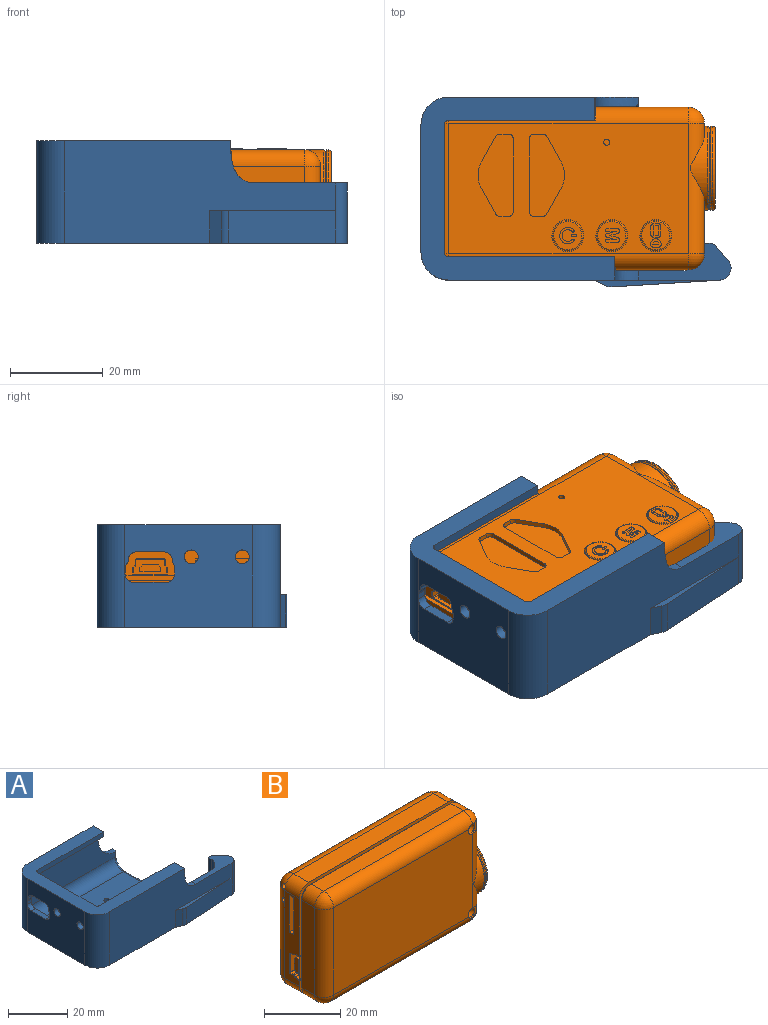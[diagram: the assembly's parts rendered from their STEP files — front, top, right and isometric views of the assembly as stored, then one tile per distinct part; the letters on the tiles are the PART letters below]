
ASSEMBLY  parts=2 mates=1
PART A: 69 faces, bbox 66.9x41x22.1 mm
  f0: plane 27.5x22.1mm, normal (-1,0,0), area 529.3mm2, adj f2,f4,f40,f41,f57,f58,f59,f60
  f1: plane 27.5x11.1mm, normal (1,0,0), area 226.8mm2, adj f33,f36,f37,f46,f57,f58,f59,f60
  f2: plane 66.93x40.96mm, normal (0,0,-1), area 1888.3mm2, adj f0,f6,f7,f8,f10,f11,f12,f13
  f3: plane 40x27.5mm, normal (0,0,1), area 1079.5mm2, adj f28,f29,f30,f31,f34,f37,f39,f51
  f4: plane 41.8x39.5mm, normal (0,0,1), area 529.1mm2, adj f0,f5,f6,f7,f21,f23,f24,f25
  f5: extruded ~5x2.17mm, area 10.8mm2, adj f4,f6,f22,f25,f48
  f6: plane 41.01x22.1mm, normal (0,1,0), area 794.4mm2, adj f2,f4,f5,f8,f22,f41
  f7: plane 58.44x22.1mm, normal (0,-1,0), area 902.9mm2, adj f2,f4,f12,f17,f19,f20,f21,f40
  f8: plane 29.43x7.84mm, normal (1,0,0), area 41.6mm2, adj f2,f6,f22,f32,f49,f50,f51
  f9: plane 40.01x11.11mm, normal (0,-1,0), area 388.3mm2, adj f22,f33,f34,f48,f49
  f10: plane 50.17x17.31mm, normal (0,1,0), area 589.1mm2, adj f2,f13,f17,f21,f26,f36,f39,f44
  f11: plane 13x3.57mm, normal (0.77,0.64,0), area 60.6mm2, adj f2,f12,f16,f17
  f12: cylinder r=2.63mm len=13mm, axis (0,0,-1), area 66.5mm2, adj f2,f7,f11,f17,f18
  f13: cylinder r=4.94mm len=13mm, axis (0,0,-1), area 96.9mm2, adj f2,f10,f14,f17
  f14: plane 13x1.37mm, normal (-1,0,0), area 17.8mm2, adj f2,f13,f15,f17
  f15: plane 13x1.07mm, normal (0,1,0), area 13.9mm2, adj f2,f14,f16,f17
  f16: cylinder r=2mm len=13mm, axis (0,0,-1), area 22.7mm2, adj f2,f11,f15,f17
  f17: plane 19.93x8mm, normal (0,0,1), area 69.6mm2, adj f7,f10,f11,f12,f13,f14,f15,f16
  f18: plane 23.18x7mm, normal (0.06,-1,0), area 162.6mm2, adj f2,f12,f20,f56
  f19: plane 7x2.43mm, normal (-0.43,-0.9,0), area 18.9mm2, adj f2,f7,f20,f56
  f20: plane 27.1x1.46mm, normal (0,0,1), area 20.3mm2, adj f7,f18,f19,f56
  f21: extruded ~9.1x5.21mm, area 31.7mm2, adj f4,f7,f10,f17,f24,f44
  f22: extruded ~12.09x9.37mm, area 35.6mm2, adj f5,f6,f8,f9,f48,f49
  f23: plane 27.5x2mm, normal (1,0,0), area 55mm2, adj f4,f42,f43,f46
  f24: plane 35.83x2.01mm, normal (0,1,0), area 71.6mm2, adj f4,f21,f42,f44
  f25: plane 31.62x2.01mm, normal (0,-1,0), area 63.1mm2, adj f4,f5,f43,f48
  f26: cylinder r=2.04mm len=6mm, axis (0,0,-1), area 14.1mm2, adj f2,f10,f27,f54,f55
  f27: plane 1x0.95mm, normal (0,-1,0), area 0.9mm2, adj f2,f26,f32,f53
  f28: cylinder r=1mm len=2mm, axis (0,0,-1), area 12.6mm2, adj f2,f3
  f29: cylinder r=1mm len=2mm, axis (0,0,-1), area 12.6mm2, adj f2,f3
  f30: cylinder r=1mm len=2mm, axis (0,0,-1), area 12.6mm2, adj f2,f3
  f31: cylinder r=1mm len=2mm, axis (0,0,-1), area 12.6mm2, adj f2,f3
  f32: cylinder r=4mm len=4mm, axis (0,0,1), area 6.3mm2, adj f2,f8,f27,f52
  f33: cylinder r=4mm len=11.1mm, axis (0,0,-1), area 69.7mm2, adj f1,f9,f35,f47
  f34: cylinder r=4mm len=40mm, axis (-1,0,0), area 251.3mm2, adj f3,f9,f35,f50
  f35: sphere r=4mm, area 25.1mm2, adj f33,f34,f37
  f36: cylinder r=4mm len=11.1mm, axis (0,0,1), area 69.7mm2, adj f1,f10,f38,f45
  f37: cylinder r=4mm len=27.5mm, axis (0,-1,0), area 172.8mm2, adj f1,f3,f35,f38
  f38: sphere r=4mm, area 25.1mm2, adj f36,f37,f39
  f39: cylinder r=4mm len=36.05mm, axis (1,0,0), area 213.1mm2, adj f3,f10,f38,f55
  f40: cylinder r=6mm len=22.1mm, axis (0,0,-1), area 208.3mm2, adj f0,f2,f4,f7
  f41: cylinder r=6mm len=22.1mm, axis (0,0,1), area 208.3mm2, adj f0,f2,f4,f6
  f42: cylinder r=1mm len=2mm, axis (0,0,-1), area 3.1mm2, adj f4,f23,f24,f45
  f43: cylinder r=1mm len=2mm, axis (0,0,1), area 3.1mm2, adj f4,f23,f25,f47
  f44: cylinder r=3mm len=36.24mm, axis (-1,0,0), area 169.3mm2, adj f10,f21,f24,f45
  f45: torus R=1mm, axis (0,0,-1), area 21.5mm2, adj f36,f42,f44,f46
  f46: cylinder r=3mm len=27.5mm, axis (0,1,0), area 129.6mm2, adj f1,f23,f45,f47
  f47: torus R=1mm, axis (0,0,-1), area 21.5mm2, adj f33,f43,f46,f48
  f48: cylinder r=3mm len=31.83mm, axis (1,0,0), area 149.4mm2, adj f5,f9,f22,f25,f47
  f49: cylinder r=1mm len=1.95mm, axis (0,0,1), area 3mm2, adj f8,f9,f22,f50
  f50: torus R=5mm, axis (1,0,0), area 10.8mm2, adj f8,f34,f49,f51
  f51: cylinder r=1mm len=23.43mm, axis (0,1,0), area 36.8mm2, adj f3,f8,f50,f52
  f52: torus R=3mm, axis (0,0,-1), area 9mm2, adj f3,f32,f51,f53
  f53: cylinder r=1mm len=1mm, axis (-1,0,0), area 1.5mm2, adj f3,f27,f52,f54
  f54: torus R=3.04mm, axis (0,0,-1), area 3.3mm2, adj f3,f26,f53,f55
  f55: bspline ~5x4.37mm, area 6.9mm2, adj f26,f39,f54
  f56: cylinder r=3mm len=7mm, axis (0,0,-1), area 10.7mm2, adj f2,f18,f19,f20
  f57: cylinder r=1.5mm len=3mm, axis (-1,0,0), area 18.8mm2, adj f0,f1
  f58: cylinder r=1.5mm len=3mm, axis (-1,0,0), area 18.8mm2, adj f0,f1
  f59: cylinder r=1.8mm len=2mm, axis (-1,0,0), area 5.7mm2, adj f0,f1,f60,f68
  f60: plane 7x2mm, normal (0,0,1), area 14mm2, adj f0,f1,f59,f61
  f61: cylinder r=1.8mm len=2mm, axis (-1,0,0), area 5.7mm2, adj f0,f1,f60,f62
  f62: plane 2x1.29mm, normal (0,1,0), area 2.6mm2, adj f0,f1,f61,f63
  f63: cylinder r=1.8mm len=2mm, axis (-1,0,0), area 2.8mm2, adj f0,f1,f62,f64
  f64: cylinder r=1.8mm len=2.23mm, axis (-1,0,0), area 6.5mm2, adj f0,f1,f63,f65
  f65: plane 5.9x2mm, normal (0,0,-1), area 11.8mm2, adj f0,f1,f64,f66
  f66: cylinder r=1.8mm len=2.13mm, axis (-1,0,0), area 6.3mm2, adj f0,f1,f65,f67
  f67: cylinder r=1.8mm len=2mm, axis (-1,0,0), area 3.2mm2, adj f0,f1,f66,f68
  f68: plane 2x1.29mm, normal (0,-1,0), area 2.6mm2, adj f0,f1,f59,f67
PART B: 231 faces, bbox 61.2x19.8x35.2 mm
  f0: cylinder r=1.5mm len=5mm, axis (0,-1,0), area 44.3mm2, adj f27,f30,f221,f227,f228,f230
  f1: cylinder r=1.5mm len=5mm, axis (0,-1,0), area 44.3mm2, adj f27,f33,f222,f223,f224,f226
  f2: plane 7.3x3.3mm, normal (-1,0,0), area 15.9mm2, adj f194,f195,f196,f197,f198,f199,f200,f201
  f3: plane 58.7x5.21mm, normal (0,-1,0), area 63.4mm2, adj f5,f10,f16,f18,f38,f39,f40,f41
  f4: plane 58.7x21.91mm, normal (0,-1,0), area 88.9mm2, adj f5,f10,f15,f19,f35,f36,f37,f38
  f5: plane 28.1x5.5mm, normal (-1,0,0), area 111.2mm2, adj f3,f4,f44,f51,f53,f168,f169,f170
  f6: plane 6.1x6.1mm, normal (0,1,0), area 23.3mm2, adj f97,f99,f100,f101,f102,f103,f104,f105
  f7: plane 6.9x6.9mm, normal (0,1,0), area 4.2mm2, adj f90,f94
  f8: plane 6.9x6.9mm, normal (0,1,0), area 4.2mm2, adj f89,f93
  f9: plane 6.9x6.9mm, normal (0,1,0), area 4.2mm2, adj f88,f91
  f10: cylinder r=9.05mm len=18.1mm, axis (-1,0,0), area 86.9mm2, adj f3,f4,f11,f12,f13,f14,f15,f16
  f11: plane 11.32x4.65mm, normal (1,0,0), area 47.1mm2, adj f10,f13,f14,f25
  f12: plane 4.65x2.52mm, normal (1,0,0), area 6.2mm2, adj f10,f13,f14,f26
  f13: cylinder r=3.5mm len=28.1mm, axis (0,0,-1), area 103.3mm2, adj f10,f11,f12,f27,f32,f34,f223,f225
  f14: plane 58.7x35.1mm, normal (0,1,0), area 160.4mm2, adj f10,f11,f12,f15,f16,f20,f21,f22
  f15: plane 9.45x1mm, normal (1,0,0), area 9.4mm2, adj f4,f10,f14,f35
  f16: plane 1x0.65mm, normal (1,0,0), area 0.6mm2, adj f3,f10,f14,f41
  f17: cylinder r=3.5mm len=28.1mm, axis (0,0,1), area 111.8mm2, adj f10,f18,f19,f42,f48,f49
  f18: plane 5.5x2.52mm, normal (1,0,0), area 6.7mm2, adj f3,f10,f17,f54
  f19: plane 11.32x5.5mm, normal (1,0,0), area 55.1mm2, adj f4,f10,f17,f50
  f20: plane 51.7x4.65mm, normal (0,0,-1), area 240.4mm2, adj f14,f24,f26,f33
  f21: plane 28.1x4.65mm, normal (-1,0,0), area 130.7mm2, adj f14,f23,f24,f29
  f22: plane 51.7x4.65mm, normal (0,0,1), area 240.4mm2, adj f14,f23,f25,f30
  f23: cylinder r=3.5mm len=4.65mm, axis (0,-1,0), area 25.6mm2, adj f14,f21,f22,f28
  f24: cylinder r=3.5mm len=4.65mm, axis (0,-1,0), area 25.6mm2, adj f14,f20,f21,f31
  f25: cylinder r=3.5mm len=4.65mm, axis (0,-1,0), area 25.6mm2, adj f11,f14,f22,f32
  f26: cylinder r=3.5mm len=4.65mm, axis (0,-1,0), area 25.6mm2, adj f12,f14,f20,f34
  f27: plane 51.7x28.1mm, normal (0,-1,0), area 1446.8mm2, adj f0,f1,f13,f29,f30,f33,f224,f230
  f28: sphere r=3.5mm, area 19.2mm2, adj f23,f29,f30
  f29: cylinder r=3.5mm len=28.1mm, axis (0,0,1), area 154.5mm2, adj f21,f27,f28,f31
  f30: cylinder r=3.5mm len=51.7mm, axis (1,0,0), area 283.1mm2, adj f0,f22,f27,f28,f32,f228
  f31: sphere r=3.5mm, area 19.2mm2, adj f24,f29,f33
  f32: sphere r=3.5mm, area 17.4mm2, adj f13,f25,f30,f227,f228
  f33: cylinder r=3.5mm len=51.7mm, axis (-1,0,0), area 283.1mm2, adj f1,f20,f27,f31,f34,f226
  f34: sphere r=3.5mm, area 17.4mm2, adj f13,f26,f33,f223,f226
  f35: cylinder r=2.5mm len=2.5mm, axis (0,1,0), area 3.9mm2, adj f4,f14,f15,f36
  f36: plane 51.7x1mm, normal (0,0,1), area 51.7mm2, adj f4,f14,f35,f37
  f37: cylinder r=2.5mm len=2.5mm, axis (0,1,0), area 3.9mm2, adj f4,f14,f36,f38
  f38: plane 28.1x1.24mm, normal (-1,0,0), area 28.2mm2, adj f3,f4,f14,f37,f39,f192,f193,f210
  f39: cylinder r=2.5mm len=2.5mm, axis (0,1,0), area 3.9mm2, adj f3,f14,f38,f40
  f40: plane 51.7x1mm, normal (0,0,-1), area 51.7mm2, adj f3,f14,f39,f41
  f41: cylinder r=2.5mm len=2.5mm, axis (0,1,0), area 3.9mm2, adj f3,f14,f16,f40
  f42: plane 51.7x28.1mm, normal (0,1,0), area 1131.3mm2, adj f17,f43,f44,f45,f66,f67,f68,f69
  f43: cylinder r=3.5mm len=51.7mm, axis (1,0,0), area 284.2mm2, adj f42,f47,f49,f55
  f44: cylinder r=3.5mm len=28.1mm, axis (0,0,-1), area 153.5mm2, adj f5,f42,f46,f47,f173
  f45: cylinder r=3.5mm len=51.7mm, axis (-1,0,0), area 284.2mm2, adj f42,f46,f48,f52
  f46: sphere r=3.5mm, area 18.2mm2, adj f44,f45,f51,f175
  f47: sphere r=3.5mm, area 19.2mm2, adj f43,f44,f53
  f48: sphere r=3.5mm, area 19.2mm2, adj f17,f45,f50
  f49: sphere r=3.5mm, area 19.2mm2, adj f17,f43,f54
  f50: cylinder r=3.5mm len=5.5mm, axis (0,-1,0), area 30.2mm2, adj f4,f19,f48,f52
  f51: cylinder r=3.5mm len=5.5mm, axis (0,-1,0), area 30.1mm2, adj f4,f5,f46,f52,f175
  f52: plane 51.7x5.5mm, normal (0,0,1), area 284.3mm2, adj f4,f45,f50,f51
  f53: cylinder r=3.5mm len=5.5mm, axis (0,-1,0), area 30.2mm2, adj f3,f5,f47,f55
  f54: cylinder r=3.5mm len=5.5mm, axis (0,-1,0), area 30.2mm2, adj f3,f18,f49,f55
  f55: plane 51.7x5.5mm, normal (0,0,-1), area 284.3mm2, adj f3,f43,f53,f54
  f56: cylinder r=8.8mm len=17.6mm, axis (1,0,0), area 0.5mm2, adj f64,f65
  f57: plane 16.9x16.9mm, normal (1,0,0), area 107.4mm2, adj f59,f63
  f58: cylinder r=9.05mm len=18.1mm, axis (-1,0,0), area 22.7mm2, adj f63,f64
  f59: cylinder r=6.1mm len=12.2mm, axis (1,0,0), area 46mm2, adj f57,f60
  f60: plane 12.2x12.2mm, normal (1,0,0), area 77.3mm2, adj f59,f61
  f61: cylinder r=3.55mm len=7.1mm, axis (1,0,0), area 2.2mm2, adj f60,f62
  f62: plane 7.1x7.1mm, normal (1,0,0), area 39.6mm2, adj f61
  f63: torus R=8.45mm, axis (1,0,0), area 52.3mm2, adj f57,f58
  f64: torus R=9.1mm, axis (1,0,0), area 23.5mm2, adj f56,f58
  f65: torus R=9.1mm, axis (-1,0,0), area 23.5mm2, adj f10,f56
  f66: cylinder r=6mm len=5.87mm, axis (0,1,0), area 6.1mm2, adj f42,f67,f75,f76
  f67: plane 5.43x3.05mm, normal (0.87,0,0.49), area 6.2mm2, adj f42,f66,f68,f76
  f68: cylinder r=1mm len=1mm, axis (0,1,0), area 1.1mm2, adj f42,f67,f69,f76
  f69: plane 1.91x1mm, normal (0,0,1), area 1.9mm2, adj f42,f68,f70,f76
  f70: cylinder r=1mm len=1mm, axis (0,1,0), area 1.6mm2, adj f42,f69,f71,f76
  f71: plane 15.75x1mm, normal (-1,0,0), area 15.7mm2, adj f42,f70,f72,f76
  f72: cylinder r=1mm len=1mm, axis (0,1,0), area 1.6mm2, adj f42,f71,f73,f76
  f73: plane 1.91x1mm, normal (0,0,-1), area 1.9mm2, adj f42,f72,f74,f76
  f74: cylinder r=1mm len=1mm, axis (0,1,0), area 1.1mm2, adj f42,f73,f75,f76
  f75: plane 5.43x3.05mm, normal (0.87,0,-0.49), area 6.2mm2, adj f42,f66,f74,f76
  f76: plane 17.75x7.6mm, normal (0,1,0), area 104mm2, adj f66,f67,f68,f69,f70,f71,f72,f73
  f77: cylinder r=6mm len=5.87mm, axis (0,1,0), area 6.1mm2, adj f42,f78,f86,f87
  f78: plane 5.43x3.05mm, normal (-0.87,0,-0.49), area 6.2mm2, adj f42,f77,f79,f87
  f79: cylinder r=1mm len=1mm, axis (0,1,0), area 1.1mm2, adj f42,f78,f80,f87
  f80: plane 1.91x1mm, normal (0,0,-1), area 1.9mm2, adj f42,f79,f81,f87
  f81: cylinder r=1mm len=1mm, axis (0,1,0), area 1.6mm2, adj f42,f80,f82,f87
  f82: plane 15.75x1mm, normal (1,0,0), area 15.7mm2, adj f42,f81,f83,f87
  f83: cylinder r=1mm len=1mm, axis (0,1,0), area 1.6mm2, adj f42,f82,f84,f87
  f84: plane 1.91x1mm, normal (0,0,1), area 1.9mm2, adj f42,f83,f85,f87
  f85: cylinder r=1mm len=1mm, axis (0,1,0), area 1.1mm2, adj f42,f84,f86,f87
  f86: plane 5.43x3.05mm, normal (-0.87,0,0.49), area 6.2mm2, adj f42,f77,f85,f87
  f87: plane 17.75x7.6mm, normal (0,1,0), area 104mm2, adj f77,f78,f79,f80,f81,f82,f83,f84
  f88: cylinder r=3.45mm len=6.9mm, axis (0,1,0), area 21.7mm2, adj f9,f42
  f89: cylinder r=3.45mm len=6.9mm, axis (0,1,0), area 21.7mm2, adj f8,f42
  f90: cylinder r=3.45mm len=6.9mm, axis (0,1,0), area 21.7mm2, adj f7,f42
  f91: cylinder r=3.25mm len=6.5mm, axis (0,-1,0), area 20.4mm2, adj f9,f98
  f92: plane 6.1x6.1mm, normal (0,1,0), area 24.9mm2, adj f98,f120,f121,f122,f123,f125,f126,f127
  f93: cylinder r=3.25mm len=6.5mm, axis (0,-1,0), area 20.4mm2, adj f8,f97
  f94: cylinder r=3.25mm len=6.5mm, axis (0,-1,0), area 20.4mm2, adj f7,f96
  f95: plane 6.1x6.1mm, normal (0,1,0), area 19.7mm2, adj f96,f130,f131,f132,f133,f134,f135,f136
  f96: torus R=3.05mm, axis (0,1,0), area 6.3mm2, adj f94,f95
  f97: torus R=3.05mm, axis (0,1,0), area 6.3mm2, adj f6,f93
  f98: torus R=3.05mm, axis (0,1,0), area 6.3mm2, adj f91,f92
  f99: extruded ~0.5x0.41mm, area 0.1mm2, adj f6,f100,f118,f119
  f100: plane 1.89x0.48mm, normal (0.25,0,0.97), area 0.2mm2, adj f6,f99,f101,f119
  f101: plane 2.05x0.1mm, normal (0,0,-1), area 0.2mm2, adj f6,f100,f102,f119
  f102: extruded ~0.34x0.27mm, area 0mm2, adj f6,f101,f103,f119
  f103: extruded ~0.34x0.27mm, area 0mm2, adj f6,f102,f104,f119
  f104: plane 2.34x0.1mm, normal (0,0,1), area 0.2mm2, adj f6,f103,f105,f119
  f105: extruded ~0.37x0.33mm, area 0.1mm2, adj f6,f104,f106,f119
  f106: plane 0.18x0.1mm, normal (-1,0,0), area 0mm2, adj f6,f105,f107,f119
  f107: extruded ~0.44x0.39mm, area 0.1mm2, adj f6,f106,f108,f119
  f108: plane 1.61x0.43mm, normal (-0.26,0,-0.97), area 0.2mm2, adj f6,f107,f109,f119
  f109: plane 1.61x0.43mm, normal (-0.26,0,0.97), area 0.2mm2, adj f6,f108,f110,f119
  f110: extruded ~0.44x0.39mm, area 0.1mm2, adj f6,f109,f111,f119
  f111: plane 0.19x0.1mm, normal (-1,0,0), area 0mm2, adj f6,f110,f112,f119
  f112: extruded ~0.37x0.33mm, area 0.1mm2, adj f6,f111,f113,f119
  f113: plane 2.34x0.1mm, normal (0,0,-1), area 0.2mm2, adj f6,f112,f114,f119
  f114: extruded ~0.34x0.27mm, area 0mm2, adj f6,f113,f115,f119
  f115: extruded ~0.34x0.27mm, area 0mm2, adj f6,f114,f116,f119
  f116: plane 2.05x0.1mm, normal (0,0,1), area 0.2mm2, adj f6,f115,f117,f119
  f117: plane 1.89x0.48mm, normal (0.25,0,-0.97), area 0.2mm2, adj f6,f116,f118,f119
  f118: extruded ~0.5x0.41mm, area 0.1mm2, adj f6,f99,f117,f119
  f119: plane 3.01x2.85mm, normal (0,1,0), area 5.9mm2, adj f99,f100,f101,f102,f103,f104,f105,f106
  f120: cylinder r=0.25mm len=0.5mm, axis (0,1,0), area 0.1mm2, adj f92,f121,f123,f124
  f121: plane 0.7x0.1mm, normal (0,0,1), area 0.1mm2, adj f92,f120,f122,f124
  f122: cylinder r=0.25mm len=0.5mm, axis (0,1,0), area 0.1mm2, adj f92,f121,f123,f124
  f123: plane 0.7x0.1mm, normal (0,0,-1), area 0.1mm2, adj f92,f120,f122,f124
  f124: plane 1.2x0.5mm, normal (0,1,0), area 0.5mm2, adj f120,f121,f122,f123
  f125: cylinder r=0.25mm len=0.44mm, axis (0,1,0), area 0.1mm2, adj f92,f126,f128,f129
  f126: cylinder r=1.25mm len=2.5mm, axis (0,1,0), area 0.6mm2, adj f92,f125,f127,f129
  f127: cylinder r=0.25mm len=0.44mm, axis (0,1,0), area 0.1mm2, adj f92,f126,f128,f129
  f128: cylinder r=1.75mm len=3.5mm, axis (0,1,0), area 0.8mm2, adj f92,f125,f127,f129
  f129: plane 3.5x3.12mm, normal (0,1,0), area 3.8mm2, adj f125,f126,f127,f128
  f130: cylinder r=0.7mm len=0.7mm, axis (0,1,0), area 0.1mm2, adj f95,f131,f137,f138
  f131: plane 0.8x0.1mm, normal (0,0,1), area 0.1mm2, adj f95,f130,f132,f138
  f132: cylinder r=0.7mm len=0.7mm, axis (0,1,0), area 0.1mm2, adj f95,f131,f133,f138
  f133: plane 1.6x0.1mm, normal (-1,0,0), area 0.2mm2, adj f95,f132,f134,f138
  f134: cylinder r=0.7mm len=0.7mm, axis (0,1,0), area 0.1mm2, adj f95,f133,f135,f138
  f135: plane 0.8x0.1mm, normal (0,0,-1), area 0.1mm2, adj f95,f134,f136,f138
  f136: cylinder r=0.7mm len=0.7mm, axis (0,1,0), area 0.1mm2, adj f95,f135,f137,f138
  f137: plane 1.6x0.1mm, normal (1,0,0), area 0.2mm2, adj f95,f130,f136,f138
  f138: plane 3x2.2mm, normal (0,1,0), area 3.8mm2, adj f130,f131,f132,f133,f134,f135,f136,f137
  f139: cylinder r=0.2mm len=0.2mm, axis (0,1,0), area 0mm2, adj f138,f140,f146,f147
  f140: plane 0.8x0.1mm, normal (0,0,1), area 0.1mm2, adj f138,f139,f141,f147
  f141: cylinder r=0.2mm len=0.2mm, axis (0,1,0), area 0mm2, adj f138,f140,f142,f147
  f142: plane 1.6x0.1mm, normal (-1,0,0), area 0.2mm2, adj f138,f141,f143,f147
  f143: cylinder r=0.2mm len=0.2mm, axis (0,1,0), area 0mm2, adj f138,f142,f144,f147
  f144: plane 0.8x0.1mm, normal (0,0,-1), area 0.1mm2, adj f138,f143,f145,f147
  f145: cylinder r=0.2mm len=0.2mm, axis (0,1,0), area 0mm2, adj f138,f144,f146,f147
  f146: plane 1.6x0.1mm, normal (1,0,0), area 0.2mm2, adj f138,f139,f145,f147
  f147: plane 2x1.2mm, normal (0,1,0), area 2.4mm2, adj f139,f140,f141,f142,f143,f144,f145,f146
  f148: cylinder r=0.7mm len=0.59mm, axis (0,1,0), area 0.1mm2, adj f95,f149,f155,f156
  f149: plane 0.28x0.1mm, normal (0,0,1), area 0mm2, adj f95,f148,f150,f156
  f150: cylinder r=0.7mm len=0.59mm, axis (0,1,0), area 0.1mm2, adj f95,f149,f151,f156
  f151: plane 0.55x0.35mm, normal (-0.85,0,0.53), area 0.1mm2, adj f95,f150,f152,f156
  f152: cylinder r=0.6mm len=0.92mm, axis (0,1,0), area 0.1mm2, adj f95,f151,f153,f156
  f153: plane 1.14x0.1mm, normal (0,0,-1), area 0.1mm2, adj f95,f152,f154,f156
  f154: cylinder r=0.6mm len=0.92mm, axis (0,1,0), area 0.1mm2, adj f95,f153,f155,f156
  f155: plane 0.55x0.35mm, normal (0.85,0,0.53), area 0.1mm2, adj f95,f148,f154,f156
  f156: plane 2.34x1.8mm, normal (0,1,0), area 2.6mm2, adj f148,f149,f150,f151,f152,f153,f154,f155
  f157: cylinder r=0.2mm len=0.17mm, axis (0,1,0), area 0mm2, adj f156,f158,f164,f165
  f158: plane 0.55x0.35mm, normal (0.85,0,-0.53), area 0.1mm2, adj f156,f157,f159,f165
  f159: cylinder r=0.1mm len=0.15mm, axis (0,1,0), area 0mm2, adj f156,f158,f160,f165
  f160: plane 1.14x0.1mm, normal (0,0,1), area 0.1mm2, adj f156,f159,f161,f165
  f161: cylinder r=0.1mm len=0.15mm, axis (0,1,0), area 0mm2, adj f156,f160,f162,f165
  f162: plane 0.55x0.35mm, normal (-0.85,0,-0.53), area 0.1mm2, adj f156,f161,f163,f165
  f163: cylinder r=0.2mm len=0.17mm, axis (0,1,0), area 0mm2, adj f156,f162,f164,f165
  f164: plane 0.28x0.1mm, normal (0,0,-1), area 0mm2, adj f156,f157,f163,f165
  f165: plane 1.34x0.8mm, normal (0,1,0), area 0.8mm2, adj f157,f158,f159,f160,f161,f162,f163,f164
  f166: cylinder r=0.65mm len=1.3mm, axis (0,1,0), area 4.1mm2, adj f42,f167
  f167: plane 1.3x1.3mm, normal (0,1,0), area 1.3mm2, adj f166
  f168: plane 10x1.5mm, normal (0,0,1), area 15mm2, adj f5,f169,f171,f172
  f169: plane 11.8x10mm, normal (0,-1,0), area 118mm2, adj f5,f168,f170,f172
  f170: plane 10x1.5mm, normal (0,0,-1), area 15mm2, adj f5,f169,f171,f172
  f171: plane 11.8x10mm, normal (0,1,0), area 118mm2, adj f5,f168,f170,f172
  f172: plane 11.8x1.5mm, normal (-1,0,0), area 17.7mm2, adj f168,f169,f170,f171
  f173: cylinder r=0.6mm len=10mm, axis (-1,0,0), area 37.5mm2, adj f5,f44,f174
  f174: plane 1.2x1.2mm, normal (-1,0,0), area 1.1mm2, adj f173
  f175: cylinder r=0.6mm len=9.96mm, axis (-1,0,0), area 36.8mm2, adj f46,f51,f176
  f176: plane 1.2x1.2mm, normal (-1,0,0), area 1.1mm2, adj f175
  f177: cylinder r=0.3mm len=0.2mm, axis (-1,0,0), area 0mm2, adj f5,f178,f193,f213
  f178: plane 1.29x0.2mm, normal (0,0,1), area 0.3mm2, adj f5,f177,f179,f213
  f179: cylinder r=0.3mm len=0.23mm, axis (-1,0,0), area 0.1mm2, adj f5,f178,f180,f213
  f180: plane 0.41x0.34mm, normal (0,-0.77,0.64), area 0.1mm2, adj f5,f179,f181,f213
  f181: cylinder r=0.3mm len=0.23mm, axis (-1,0,0), area 0.1mm2, adj f5,f180,f182,f213
  f182: plane 0.91x0.2mm, normal (0,0,1), area 0.2mm2, adj f5,f181,f183,f213
  f183: cylinder r=0.3mm len=0.3mm, axis (-1,0,0), area 0.1mm2, adj f5,f182,f184,f213
  f184: plane 5.9x0.2mm, normal (0,-1,0), area 1.2mm2, adj f5,f183,f185,f213
  f185: cylinder r=0.3mm len=0.3mm, axis (-1,0,0), area 0.1mm2, adj f5,f184,f186,f213
  f186: plane 0.92x0.2mm, normal (0,0,-1), area 0.2mm2, adj f5,f185,f187,f213
  f187: cylinder r=0.3mm len=0.2mm, axis (-1,0,0), area 0mm2, adj f5,f186,f188,f213
  f188: plane 0.41x0.34mm, normal (0,-0.64,-0.77), area 0.1mm2, adj f5,f187,f189,f213
  f189: cylinder r=0.3mm len=0.2mm, axis (-1,0,0), area 0mm2, adj f5,f188,f190,f213
  f190: plane 1.29x0.2mm, normal (0,0,-1), area 0.3mm2, adj f5,f189,f191,f213
  f191: cylinder r=0.3mm len=0.2mm, axis (-1,0,0), area 0mm2, adj f5,f190,f192,f213
  f192: cylinder r=0.2mm len=1mm, axis (-1,0,0), area 0.4mm2, adj f4,f5,f38,f191,f210
  f193: cylinder r=0.2mm len=1mm, axis (-1,0,0), area 0.4mm2, adj f3,f5,f38,f177,f212
  f194: plane 5.9x4.8mm, normal (0,-1,0), area 28.3mm2, adj f2,f195,f209,f213
  f195: cylinder r=0.15mm len=4.8mm, axis (-1,0,0), area 1.1mm2, adj f2,f194,f196,f213
  f196: plane 4.8x0.91mm, normal (0,0,1), area 4.4mm2, adj f2,f195,f197,f213
  f197: cylinder r=0.45mm len=4.8mm, axis (-1,0,0), area 1.9mm2, adj f2,f196,f198,f213
  f198: plane 4.8x0.41mm, normal (0,-0.77,0.64), area 2.5mm2, adj f2,f197,f199,f213
  f199: cylinder r=0.15mm len=4.8mm, axis (-1,0,0), area 0.6mm2, adj f2,f198,f200,f213
  f200: plane 4.8x1.29mm, normal (0,0,1), area 6.2mm2, adj f2,f199,f201,f213
  f201: cylinder r=0.15mm len=4.8mm, axis (-1,0,0), area 1.1mm2, adj f2,f200,f202,f213
  f202: plane 7x4.8mm, normal (0,1,0), area 33.6mm2, adj f2,f201,f203,f213
  f203: cylinder r=0.15mm len=4.8mm, axis (-1,0,0), area 1.1mm2, adj f2,f202,f204,f213
  f204: plane 4.8x1.29mm, normal (0,0,-1), area 6.2mm2, adj f2,f203,f205,f213
  f205: cylinder r=0.15mm len=4.8mm, axis (-1,0,0), area 0.5mm2, adj f2,f204,f206,f213
  f206: plane 4.8x0.41mm, normal (0,-0.64,-0.77), area 2.5mm2, adj f2,f205,f207,f213
  f207: cylinder r=0.45mm len=4.8mm, axis (-1,0,0), area 1.5mm2, adj f2,f206,f208,f213
  f208: plane 4.8x0.92mm, normal (0,0,-1), area 4.4mm2, adj f2,f207,f209,f213
  f209: cylinder r=0.15mm len=4.8mm, axis (-1,0,0), area 1.1mm2, adj f2,f194,f208,f213
  f210: cylinder r=0.3mm len=0.8mm, axis (-1,0,0), area 0.3mm2, adj f38,f192,f211,f213
  f211: plane 7x0.8mm, normal (0,-1,0), area 5.6mm2, adj f38,f210,f212,f213
  f212: cylinder r=0.3mm len=0.8mm, axis (-1,0,0), area 0.3mm2, adj f38,f193,f211,f213
  f213: plane 7.6x3.6mm, normal (-1,0,0), area 3.1mm2, adj f177,f178,f179,f180,f181,f182,f183,f184
  f214: plane 4.5x3.5mm, normal (0,1,0), area 15.7mm2, adj f2,f215,f218,f219
  f215: plane 4.5x0.5mm, normal (0,0.71,-0.71), area 3.2mm2, adj f2,f214,f216,f218
  f216: plane 4.5x1mm, normal (0,0,-1), area 4.5mm2, adj f2,f215,f217,f218
  f217: plane 4.5x4.5mm, normal (0,-1,0), area 20.2mm2, adj f2,f216,f218,f220
  f218: plane 4.5x1.5mm, normal (-1,0,0), area 6.5mm2, adj f214,f215,f216,f217,f219,f220
  f219: plane 4.5x0.5mm, normal (0,0.71,0.71), area 3.2mm2, adj f2,f214,f218,f220
  f220: plane 4.5x1mm, normal (0,0,1), area 4.5mm2, adj f2,f217,f218,f219
  f221: plane 3x3mm, normal (0,-1,0), area 7.1mm2, adj f0
  f222: plane 3x3mm, normal (0,-1,0), area 7.1mm2, adj f1
  f223: plane 3.11x2.27mm, normal (0,-1,0), area 2.9mm2, adj f1,f13,f34,f224,f225,f226
  f224: plane 0.6x0.01mm, normal (1,0,0), area 0mm2, adj f1,f27,f223,f225
  f225: plane 1.96x0.6mm, normal (0,0,-1), area 0.8mm2, adj f13,f223,f224
  f226: plane 1.91x0.47mm, normal (0,0,1), area 0.6mm2, adj f1,f33,f34,f223
  f227: plane 3.11x2.27mm, normal (0,-1,0), area 2.9mm2, adj f0,f13,f32,f228,f229,f230
  f228: plane 1.91x0.47mm, normal (0,0,-1), area 0.6mm2, adj f0,f30,f32,f227
  f229: plane 1.96x0.6mm, normal (0,0,1), area 0.8mm2, adj f13,f227,f230
  f230: plane 0.6x0.01mm, normal (1,0,0), area 0mm2, adj f0,f27,f227,f229
PLACE A t=(-38.72,-13.12,-14.48)mm
PLACE B rot(axis=(1,0,0),90deg) t=(-8.87,-13.12,-14.46)mm
MATE fastened B.f27 <-> A.f3  axis (0,0,-1) through (-34.72,-13.12,-23.53)mm
